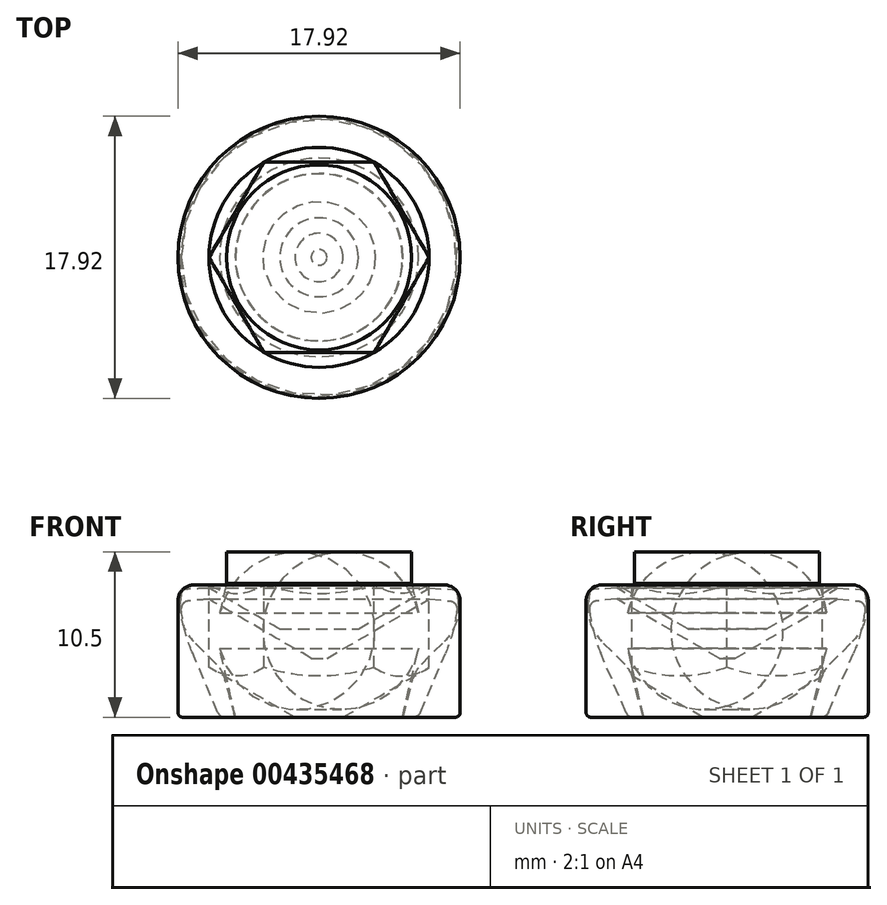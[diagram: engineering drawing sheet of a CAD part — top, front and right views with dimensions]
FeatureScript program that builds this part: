
annotation { "Feature Type Name" : "Feature", "Feature Type Description" : "" }
export const myFeature = defineFeature(function(context is Context, id is Id, definition is map)
    precondition{}
    {
        {
            var Q0;
            Q0=qCreatedBy(makeId("Front.planeOp"),FACE);
            var sketch = newSketch(context, id + "F0", { "sketchPlane" : qUnion([Q0])});
            skLineSegment(sketch, "E0", {"start": v(0, 0) * mm, "end": v(0, 8.4) * mm});
            skLineSegment(sketch, "E1", {"start": v(0, 8.4) * mm, "end": v(7.96, 8.4) * mm});
            skLineSegment(sketch, "E2", {"start": v(8.96, 7.4) * mm, "end": v(8.96, 0.3) * mm});
            skLineSegment(sketch, "E3", {"start": v(8.66, 0) * mm, "end": v(0, 0) * mm});
            skPoint(sketch, "E4.visualSharp", {"position": v(8.96, 8.4) * mm});
            skArc(sketch, "E4.filletArc", {"start": v(8.96, 7.4) * mm, "mid": v(8.67, 8.1) * mm, "end": v(7.96, 8.4) * mm});
            skPoint(sketch, "E5.visualSharp", {"position": v(8.96, 0) * mm});
            skArc(sketch, "E5.filletArc", {"start": v(8.66, 0) * mm, "mid": v(8.87, 0.09) * mm, "end": v(8.96, 0.3) * mm});
            skLineSegment(sketch, "E6", {"start": v(0, 0) * mm, "end": v(0, 8.4) * mm, "construction": true});
            skSolve(sketch);
        }
        {
            var Q0;
            Q0 = qSketchRegion(id + "F0", true);
            var Q1;
            Q1=sQuery(id+"F0.wireOp",EDGE,"E0");
            revolve(context, id + "F1", {"entities" : qUnion([Q0]), "axis" : qUnion([Q1]), "revolveType" : RevolveType.FULL});
        }
        {
            var Q0;
            Q0=makeQuery(id+"F1.opRevolve","SWEPT_FACE",FACE,{"disambiguationData":[OSD([sQuery(id+"F0.wireOp",EDGE,"E1")])]});
            var sketch = newSketch(context, id + "F2", { "sketchPlane" : qUnion([Q0])});
            skCircle(sketch, "E7.cCircle", {"center": v(0, 0) * mm, "radius": 6.05 * mm, "construction": true});
            skLineSegment(sketch, "E7.0", {"start": v(-3.5, 6.05) * mm, "end": v(3.5, 6.05) * mm});
            skLineSegment(sketch, "E7.1", {"start": v(3.5, 6.05) * mm, "end": v(6.99, 0) * mm});
            skLineSegment(sketch, "E7.2", {"start": v(6.99, 0) * mm, "end": v(3.5, -6.05) * mm});
            skLineSegment(sketch, "E7.3", {"start": v(3.5, -6.05) * mm, "end": v(-3.5, -6.05) * mm});
            skLineSegment(sketch, "E7.4", {"start": v(-3.5, -6.05) * mm, "end": v(-6.99, 0) * mm});
            skLineSegment(sketch, "E7.5", {"start": v(-6.99, 0) * mm, "end": v(-3.5, 6.05) * mm});
            skPoint(sketch, "E7.0.midPoint", {"position": v(0, 6.05) * mm});
            skSolve(sketch);
        }
        {
            var Q0;
            Q0 = qSketchRegion(id + "F2", true);
            extrude(context, id + "F3", {"entities" : qUnion([Q0]), "operationType" : NewBodyOperationType.REMOVE, "oppositeDirection" : true, "offsetDistance" : 25 * mm, "depth" : 5.25 * mm, "hasSecondDirection" : true, "secondDirectionOppositeDirection" : false, "secondDirectionDepth" : 25 * mm});
        }
        {
            var Q0;
            Q0=qCreatedBy(makeId("Front.planeOp"),FACE);
            var sketch = newSketch(context, id + "F4", { "sketchPlane" : qUnion([Q0])});
            skLineSegment(sketch, "E8", {"start": v(0, -0.02) * mm, "end": v(1.5, -0.02) * mm});
            skLineSegment(sketch, "E9", {"start": v(1.5, -0.02) * mm, "end": v(6.99, 3.15) * mm});
            skLineSegment(sketch, "E10", {"start": v(6.99, 3.15) * mm, "end": v(0, 3.15) * mm});
            skLineSegment(sketch, "E11", {"start": v(0, -0.02) * mm, "end": v(0, 3.15) * mm, "construction": true});
            skLineSegment(sketch, "E12", {"start": v(0, 3.15) * mm, "end": v(0, -0.02) * mm});
            skSolve(sketch);
        }
        {
            var Q0;
            Q0 = qSketchRegion(id + "F4", true);
            var Q1;
            Q1=sQuery(id+"F4.wireOp",EDGE,"E12");
            revolve(context, id + "F5", {"operationType" : NewBodyOperationType.REMOVE, "entities" : qUnion([Q0]), "axis" : qUnion([Q1]), "revolveType" : RevolveType.FULL, "oppositeDirection" : true});
        }
        {
            var Q0;
            Q0=makeQuery(id+"F1.opRevolve","SWEPT_FACE",FACE,{"disambiguationData":[OSD([sQuery(id+"F0.wireOp",EDGE,"E1")])]});
            var sketch = newSketch(context, id + "F6", { "sketchPlane" : qUnion([Q0])});
            skCircle(sketch, "E13.cCircle", {"center": v(0, 0) * mm, "radius": 6.05 * mm, "construction": true});
            skLineSegment(sketch, "E13.0", {"start": v(-3.5, 6.05) * mm, "end": v(3.5, 6.05) * mm});
            skLineSegment(sketch, "E13.1", {"start": v(3.5, 6.05) * mm, "end": v(6.99, 0) * mm});
            skLineSegment(sketch, "E13.2", {"start": v(6.99, 0) * mm, "end": v(3.5, -6.05) * mm});
            skLineSegment(sketch, "E13.3", {"start": v(3.5, -6.05) * mm, "end": v(-3.5, -6.05) * mm});
            skLineSegment(sketch, "E13.4", {"start": v(-3.5, -6.05) * mm, "end": v(-6.99, 0) * mm});
            skLineSegment(sketch, "E13.5", {"start": v(-6.99, 0) * mm, "end": v(-3.5, 6.05) * mm});
            skPoint(sketch, "E13.0.midPoint", {"position": v(0, 6.05) * mm});
            skCircle(sketch, "E14", {"center": v(0, 0) * mm, "radius": 7.96 * mm});
            skSolve(sketch);
        }
        {
            var Q0;
            Q0=makeQuery(id+"F6.imprint","IMPRINT",FACE,{"disambiguationData":[TD([[makeQuery(id+"F6.imprint","IMPRINT",EDGE,{"derivedFrom":sQuery(id+"F6.wireOp",EDGE,"E13.0")}),-1.0]])]});
            var Q1;
            Q1=makeQuery(id+"F5.boolean.opBoolean","COPY",FACE,{"derivedFrom":makeQuery(id+"F5.opRevolve","SWEPT_FACE",FACE,{"disambiguationData":[OSD([sQuery(id+"F4.wireOp",EDGE,"E9")])]})});
            extrude(context, id + "F7", {"entities" : qUnion([Q0]), "operationType" : NewBodyOperationType.ADD, "endBound" : BoundingType.UP_TO_SURFACE, "oppositeDirection" : true, "endBoundEntityFace" : qUnion([Q1]), "depth" : 25 * mm});
        }
        {
            var Q0;
            Q0=makeQuery(id+"F1.opRevolve","SWEPT_FACE",FACE,{"disambiguationData":[OSD([sQuery(id+"F0.wireOp",EDGE,"E1")])]});
            var sketch = newSketch(context, id + "F8", { "sketchPlane" : qUnion([Q0])});
            skCircle(sketch, "E15", {"center": v(0, 0) * mm, "radius": 6.99 * mm});
            skSolve(sketch);
        }
        {
            var Q0;
            Q0 = qSketchRegion(id + "F8", true);
            extrude(context, id + "F9", {"entities" : qUnion([Q0]), "operationType" : NewBodyOperationType.REMOVE, "oppositeDirection" : true, "depth" : 2 * mm, "hasDraft" : true, "draftAngle" : 60 * degree, "draftPullDirection" : true});
        }
        {
            var Q0;
            Q0=qCreatedBy(makeId("Front.planeOp"),FACE);
            var sketch = newSketch(context, id + "F10", { "sketchPlane" : qUnion([Q0])});
            skLineSegment(sketch, "E16", {"start": v(0, 0) * mm, "end": v(0, 3.75) * mm});
            skLineSegment(sketch, "E17", {"start": v(8.02, 4.04) * mm, "end": v(6.43, 0.3) * mm});
            skLineSegment(sketch, "E18", {"start": v(5.97, 0) * mm, "end": v(0, 0) * mm});
            skPoint(sketch, "E19.visualSharp", {"position": v(6.3, 0) * mm});
            skArc(sketch, "E19.filletArc", {"start": v(5.97, 0) * mm, "mid": v(6.25, 0.08) * mm, "end": v(6.43, 0.3) * mm});
            skLineSegment(sketch, "E20", {"start": v(0, 3.75) * mm, "end": v(0, 0) * mm, "construction": true});
            skLineSegment(sketch, "E21", {"start": v(0, 3.75) * mm, "end": v(0.5, 3.75) * mm});
            skLineSegment(sketch, "E22", {"start": v(0.5, 3.75) * mm, "end": v(7, 7.5) * mm});
            skLineSegment(sketch, "E23", {"start": v(7, 7.5) * mm, "end": v(8.3, 7.39) * mm});
            skArc(sketch, "E24.filletArc", {"start": v(8.02, 4.04) * mm, "mid": v(8.49, 5.4) * mm, "end": v(8.75, 6.83) * mm});
            skPoint(sketch, "E25.visualSharp", {"position": v(8.8, 7.34) * mm});
            skArc(sketch, "E25.filletArc", {"start": v(8.75, 6.83) * mm, "mid": v(8.64, 7.2) * mm, "end": v(8.3, 7.39) * mm});
            skLineSegment(sketch, "E26", {"start": v(8.02, 4.04) * mm, "end": v(8.85, 6) * mm, "construction": true});
            skSolve(sketch);
        }
        {
            var Q0;
            Q0 = qSketchRegion(id + "F10", true);
            var Q1;
            Q1=sQuery(id+"F10.wireOp",EDGE,"E16");
            revolve(context, id + "F11", {"entities" : qUnion([Q0]), "axis" : qUnion([Q1]), "revolveType" : RevolveType.FULL});
        }
        {
            var Q0;
            Q0=qCreatedBy(makeId("Front.planeOp"),FACE);
            var sketch = newSketch(context, id + "F12", { "sketchPlane" : qUnion([Q0])});
            skLineSegment(sketch, "E27", {"start": v(0, 0) * mm, "end": v(0, 10.5) * mm});
            skLineSegment(sketch, "E28", {"start": v(0, 10.5) * mm, "end": v(5.88, 10.5) * mm});
            skLineSegment(sketch, "E29", {"start": v(5.88, 10.5) * mm, "end": v(5.88, 8.5) * mm});
            skLineSegment(sketch, "E30", {"start": v(5.88, 8.5) * mm, "end": v(6.3, 6.62) * mm});
            skLineSegment(sketch, "E31", {"start": v(6.3, 4.37) * mm, "end": v(5.3, 0) * mm});
            skLineSegment(sketch, "E32", {"start": v(5.3, 0) * mm, "end": v(0, 0) * mm});
            skLineSegment(sketch, "E33", {"start": v(0, 10.5) * mm, "end": v(0, 0) * mm, "construction": true});
            skPoint(sketch, "E34.visualSharp", {"position": v(6.57, 5.5) * mm});
            skArc(sketch, "E34.filletArc", {"start": v(6.3, 4.37) * mm, "mid": v(6.44, 5.5) * mm, "end": v(6.3, 6.62) * mm});
            skSolve(sketch);
        }
        {
            var Q0;
            Q0 = qSketchRegion(id + "F12", true);
            var Q1;
            Q1=sQuery(id+"F12.wireOp",EDGE,"E27");
            revolve(context, id + "F13", {"entities" : qUnion([Q0]), "axis" : qUnion([Q1]), "revolveType" : RevolveType.FULL});
        }
        {
            var Q0;
            Q0=qCreatedBy(makeId("Front.planeOp"),FACE);
            var sketch = newSketch(context, id + "F14", { "sketchPlane" : qUnion([Q0])});
            skLineSegment(sketch, "E35", {"start": v(0, 0) * mm, "end": v(0, 5.6) * mm});
            skLineSegment(sketch, "E36", {"start": v(7.97, 4.82) * mm, "end": v(6.5, 3.35) * mm});
            skLineSegment(sketch, "E37", {"start": v(5.32, 0) * mm, "end": v(0, 0) * mm});
            skPoint(sketch, "E38.visualSharp", {"position": v(5.32, 0) * mm});
            skLineSegment(sketch, "E39", {"start": v(0, 5.6) * mm, "end": v(0, 0) * mm, "construction": true});
            skLineSegment(sketch, "E40", {"start": v(0, 5.6) * mm, "end": v(2.5, 5.6) * mm});
            skLineSegment(sketch, "E41", {"start": v(2.5, 5.6) * mm, "end": v(7, 8.2) * mm});
            skLineSegment(sketch, "E42", {"start": v(7, 8.2) * mm, "end": v(8.47, 8.12) * mm});
            skLineSegment(sketch, "E43", {"start": v(5.32, 0) * mm, "end": v(5.98, 2.45) * mm});
            skLineSegment(sketch, "E44", {"start": v(8.75, 7.87) * mm, "end": v(8.81, 7.41) * mm});
            skPoint(sketch, "E45.visualSharp", {"position": v(8.72, 8.11) * mm});
            skArc(sketch, "E45.filletArc", {"start": v(8.75, 7.87) * mm, "mid": v(8.66, 8.04) * mm, "end": v(8.47, 8.12) * mm});
            skLineSegment(sketch, "E46", {"start": v(8.65, 5.5) * mm, "end": v(9.03, 5.88) * mm, "construction": true});
            skLineSegment(sketch, "E47", {"start": v(8.81, 7.41) * mm, "end": v(8.82, 7.36) * mm});
            skPoint(sketch, "E48.visualSharp", {"position": v(9.03, 5.88) * mm});
            skArc(sketch, "E48.filletArc", {"start": v(7.97, 4.82) * mm, "mid": v(8.7, 6) * mm, "end": v(8.82, 7.36) * mm});
            skPoint(sketch, "E49.visualSharp", {"position": v(6.12, 2.97) * mm});
            skArc(sketch, "E49.filletArc", {"start": v(6.5, 3.35) * mm, "mid": v(6.18, 2.94) * mm, "end": v(5.98, 2.45) * mm});
            skSolve(sketch);
        }
        {
            var Q0;
            Q0 = qSketchRegion(id + "F14", true);
            var Q1;
            Q1=sQuery(id+"F14.wireOp",EDGE,"E35");
            revolve(context, id + "F15", {"entities" : qUnion([Q0]), "axis" : qUnion([Q1]), "revolveType" : RevolveType.FULL});
        }
    });
